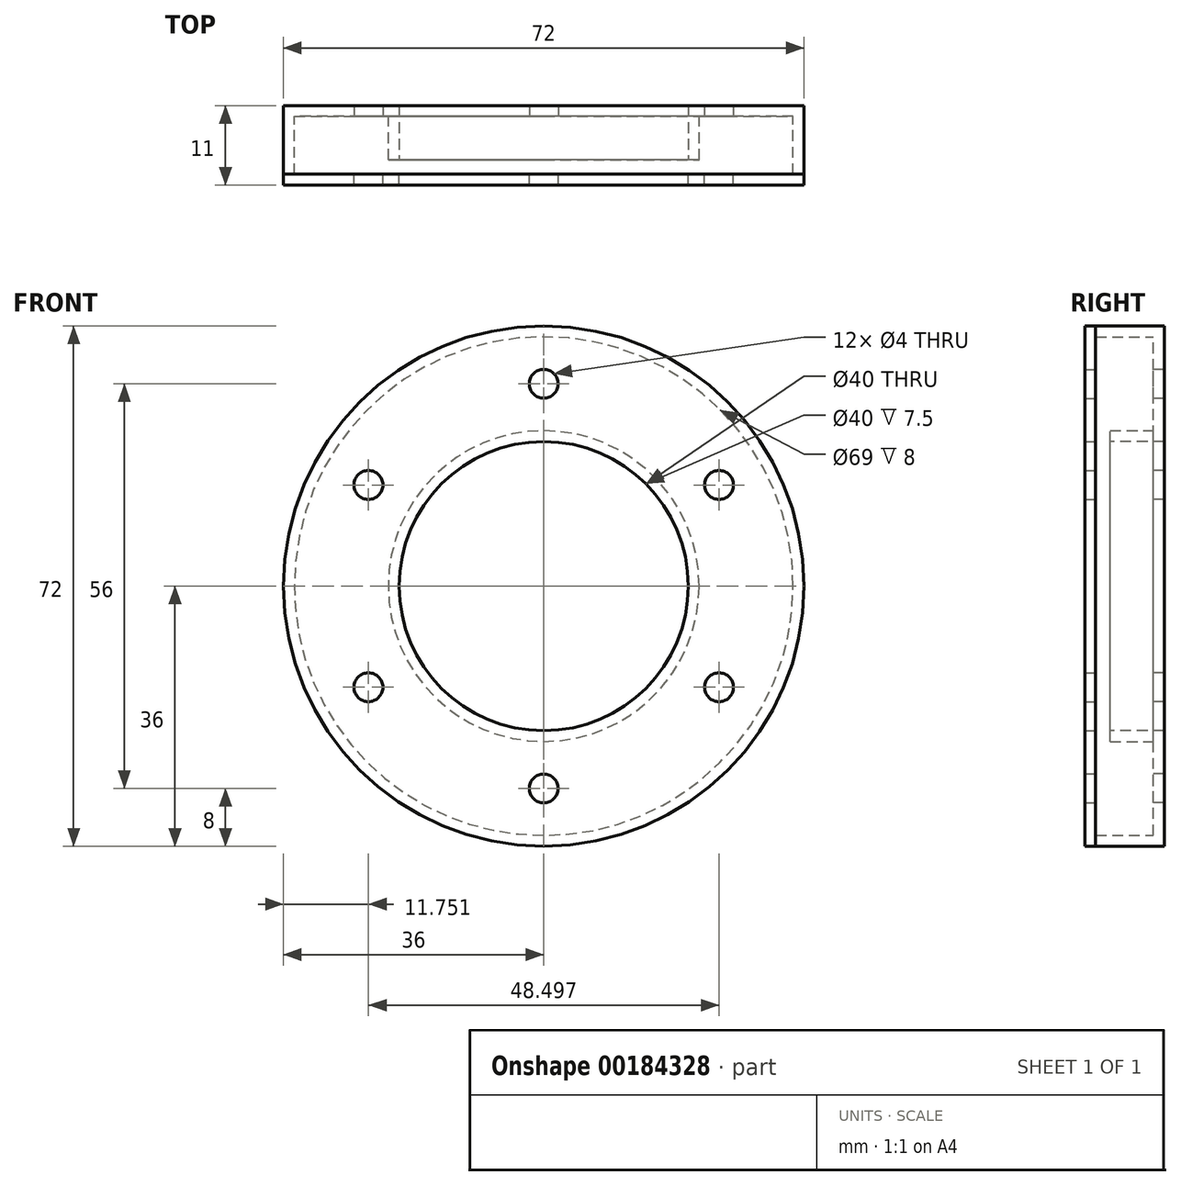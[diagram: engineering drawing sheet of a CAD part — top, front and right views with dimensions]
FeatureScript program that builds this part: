
annotation { "Feature Type Name" : "Feature", "Feature Type Description" : "" }
export const myFeature = defineFeature(function(context is Context, id is Id, definition is map)
    precondition{}
    {
        {
            var Q0;
            Q0=qCreatedBy(makeId("Front.planeOp"),FACE);
            var sketch = newSketch(context, id + "F0", { "sketchPlane" : qUnion([Q0])});
            skCircle(sketch, "E0", {"center": v(0, 28) * mm, "radius": 6 * mm, "construction": true});
            skCircle(sketch, "E1", {"center": v(0, 0) * mm, "radius": 20 * mm});
            skCircle(sketch, "E2", {"center": v(0, 0) * mm, "radius": 21.5 * mm});
            skCircle(sketch, "E3", {"center": v(0, 0) * mm, "radius": 34.5 * mm});
            skCircle(sketch, "E4", {"center": v(0, 0) * mm, "radius": 36 * mm});
            skPoint(sketch, "E5.1.0", {"position": v(-24.25, 14) * mm});
            skPoint(sketch, "E5.2.0", {"position": v(-24.25, -14) * mm});
            skPoint(sketch, "E5.3.0", {"position": v(0, -28) * mm});
            skPoint(sketch, "E5.4.0", {"position": v(24.25, -14) * mm});
            skPoint(sketch, "E5.5.0", {"position": v(24.25, 14) * mm});
            skSolve(sketch);
        }
        {
            var Q0;
            Q0=makeQuery(id+"F0.imprint","IMPRINT",FACE,{"disambiguationData":[TD([[makeQuery(id+"F0.imprint","IMPRINT",EDGE,{"derivedFrom":sQuery(id+"F0.wireOp",EDGE,"E0")}),-1.0]])]});
            var Q1;
            Q1=makeQuery(id+"F0.imprint","IMPRINT",FACE,{"disambiguationData":[TD([[makeQuery(id+"F0.imprint","IMPRINT",EDGE,{"derivedFrom":sQuery(id+"F0.wireOp",EDGE,"E1")}),-1.0]])]});
            var Q2;
            Q2=makeQuery(id+"F0.imprint","IMPRINT",FACE,{"disambiguationData":[TD([[makeQuery(id+"F0.imprint","IMPRINT",EDGE,{"derivedFrom":sQuery(id+"F0.wireOp",EDGE,"E0")}),1.0]])]});
            var Q3;
            Q3=makeQuery(id+"F0.imprint","IMPRINT",FACE,{"disambiguationData":[TD([[makeQuery(id+"F0.imprint","IMPRINT",EDGE,{"derivedFrom":sQuery(id+"F0.wireOp",EDGE,"E3")}),-1.0]])]});
            var Q4;
            Q4=makeQuery(id+"F0.imprint","IMPRINT",FACE,{"disambiguationData":[TD([[makeQuery(id+"F0.imprint","IMPRINT",EDGE,{"derivedFrom":sQuery(id+"F0.wireOp",EDGE,"E2")}),-1.0]])]});
            extrude(context, id + "F1", {"entities" : qUnion([Q0, Q1, Q2, Q3, Q4]), "oppositeDirection" : true, "depth" : 1.5 * mm});
        }
        {
            var Q0;
            Q0=makeQuery(id+"F0.imprint","IMPRINT",FACE,{"disambiguationData":[TD([[makeQuery(id+"F0.imprint","IMPRINT",EDGE,{"derivedFrom":sQuery(id+"F0.wireOp",EDGE,"E1")}),-1.0]])]});
            extrude(context, id + "F2", {"entities" : qUnion([Q0]), "operationType" : NewBodyOperationType.ADD, "depth" : 6 * mm});
        }
        {
            var Q0;
            Q0=makeQuery(id+"F0.imprint","IMPRINT",FACE,{"disambiguationData":[TD([[makeQuery(id+"F0.imprint","IMPRINT",EDGE,{"derivedFrom":sQuery(id+"F0.wireOp",EDGE,"E3")}),-1.0]])]});
            extrude(context, id + "F3", {"entities" : qUnion([Q0]), "operationType" : NewBodyOperationType.ADD, "depth" : 8 * mm});
        }
        {
            var Q0;
            Q0=sQuery(id+"F0.wireOp",VERTEX,"E0.center");
            var Q1;
            Q1=sQuery(id+"F0.wireOp",VERTEX,"E5.5.0");
            var Q2;
            Q2=sQuery(id+"F0.wireOp",VERTEX,"E5.4.0");
            var Q3;
            Q3=sQuery(id+"F0.wireOp",VERTEX,"E5.3.0");
            var Q4;
            Q4=sQuery(id+"F0.wireOp",VERTEX,"E5.2.0");
            var Q5;
            Q5=sQuery(id+"F0.wireOp",VERTEX,"E5.1.0");
            var Q6;
            Q6=makeQuery(id+"F1.opExtrude","SWEPT_BODY",BODY,{"disambiguationData":[OSD([sQuery(id+"F0.wireOp",EDGE,"E1"),sQuery(id+"F0.wireOp",EDGE,"E4")])]});
            hole(context, id + "F4", {"style" : HoleStyle.SIMPLE, "endStyle" : HoleEndStyle.THROUGH, "holeDiameter" : 4 * mm, "locations" : qUnion([Q0, Q1, Q2, Q3, Q4, Q5]), "scope" : qUnion([Q6]), "isTappedThrough" : true});
        }
        {
            var Q0;
            Q0=makeQuery(id+"F3.opExtrude","CAP_FACE",FACE,{"disambiguationData":[OSD([sQuery(id+"F0.wireOp",EDGE,"E3"),sQuery(id+"F0.wireOp",EDGE,"E4")])],"isStart":false});
            var sketch = newSketch(context, id + "F5", { "sketchPlane" : qUnion([Q0])});
            skCircle(sketch, "E6", {"center": v(0, 0) * mm, "radius": 34.5 * mm});
            skPoint(sketch, "E7", {"position": v(0, 28) * mm});
            skPoint(sketch, "E8.1.0", {"position": v(-24.25, 14) * mm});
            skPoint(sketch, "E8.2.0", {"position": v(-24.25, -14) * mm});
            skPoint(sketch, "E8.3.0", {"position": v(0, -28) * mm});
            skPoint(sketch, "E8.4.0", {"position": v(24.25, -14) * mm});
            skPoint(sketch, "E8.5.0", {"position": v(24.25, 14) * mm});
            skCircle(sketch, "E9", {"center": v(0, 0) * mm, "radius": 20 * mm});
            skSolve(sketch);
        }
        {
            var Q0;
            Q0=makeQuery(id+"F5.imprint","IMPRINT",FACE,{"disambiguationData":[TD([[makeQuery(id+"F5.imprint","IMPRINT",EDGE,{"derivedFrom":sQuery(id+"F5.wireOp",EDGE,"E6")}),1.0]])]});
            var Q1;
            Q1=makeQuery(id+"F5.imprint","IMPRINT",FACE,{"disambiguationData":[TD([[makeQuery(id+"F5.imprint","IMPRINT",EDGE,{"derivedFrom":sQuery(id+"F5.wireOp",EDGE,"E6")}),-1.0]])]});
            extrude(context, id + "F6", {"entities" : qUnion([Q0, Q1]), "depth" : 1.5 * mm});
        }
        {
            var Q0;
            Q0=sQuery(id+"F5.wireOp",VERTEX,"E8.5.0");
            var Q1;
            Q1=sQuery(id+"F5.wireOp",VERTEX,"E8.4.0");
            var Q2;
            Q2=sQuery(id+"F5.wireOp",VERTEX,"E8.3.0");
            var Q3;
            Q3=sQuery(id+"F5.wireOp",VERTEX,"E8.2.0");
            var Q4;
            Q4=sQuery(id+"F5.wireOp",VERTEX,"E8.1.0");
            var Q5;
            Q5=sQuery(id+"F5.wireOp",VERTEX,"E7");
            var Q6;
            Q6=makeQuery(id+"F6.opExtrude","SWEPT_BODY",BODY,{"disambiguationData":[OSD([sQuery(id+"F0.wireOp",EDGE,"E4")])]});
            hole(context, id + "F7", {"style" : HoleStyle.SIMPLE, "endStyle" : HoleEndStyle.THROUGH, "oppositeDirection" : true, "holeDiameter" : 4 * mm, "locations" : qUnion([Q0, Q1, Q2, Q3, Q4, Q5]), "scope" : qUnion([Q6]), "isTappedThrough" : true});
        }
    });
